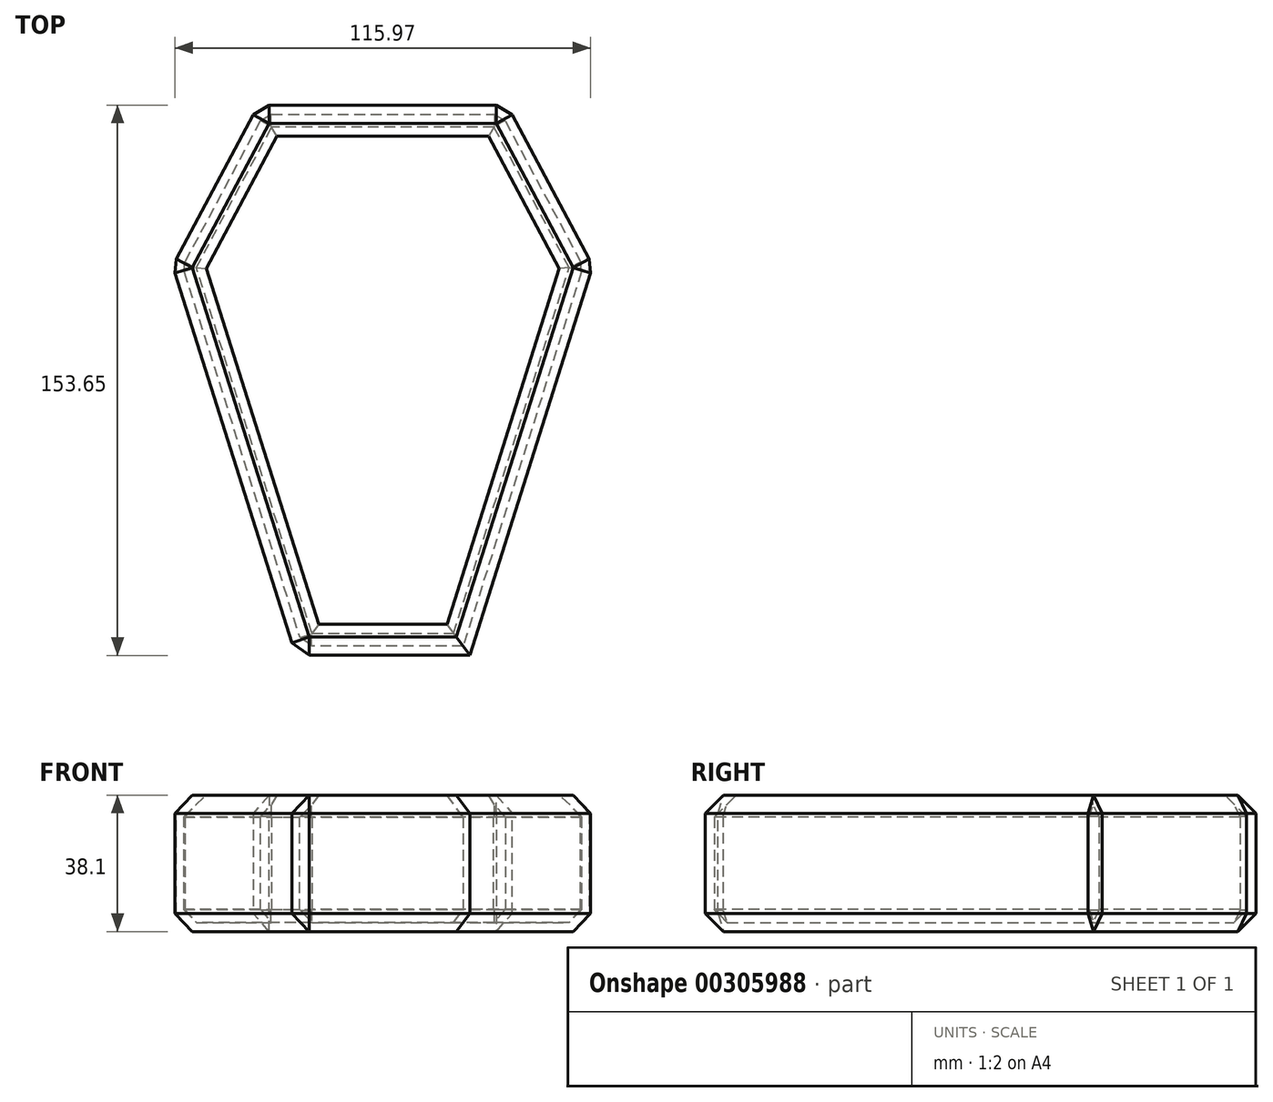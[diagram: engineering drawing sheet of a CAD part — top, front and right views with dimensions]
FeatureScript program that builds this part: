
annotation { "Feature Type Name" : "Feature", "Feature Type Description" : "" }
export const myFeature = defineFeature(function(context is Context, id is Id, definition is map)
    precondition{}
    {
        {
            var Q0;
            Q0=qCreatedBy(makeId("Top.planeOp"),FACE);
            var sketch = newSketch(context, id + "F0", { "sketchPlane" : qUnion([Q0])});
            skLineSegment(sketch, "E0", {"start": v(-34.33, -77.98) * mm, "end": v(-68.7, 30.86) * mm});
            skLineSegment(sketch, "E1", {"start": v(-68.7, 30.86) * mm, "end": v(-44.78, 75.67) * mm});
            skLineSegment(sketch, "E2", {"start": v(-34.33, -77.98) * mm, "end": v(-10.07, -77.98) * mm});
            skLineSegment(sketch, "E3", {"start": v(-44.78, 75.67) * mm, "end": v(-10.07, 75.67) * mm});
            skLineSegment(sketch, "E4.MirrorCS", {"start": v(24.63, 75.67) * mm, "end": v(-10.07, 75.67) * mm});
            skLineSegment(sketch, "E5.MirrorCS", {"start": v(48.56, 30.86) * mm, "end": v(24.63, 75.67) * mm});
            skLineSegment(sketch, "E6.MirrorCS", {"start": v(14.19, -77.98) * mm, "end": v(48.56, 30.86) * mm});
            skLineSegment(sketch, "E7.MirrorCS", {"start": v(14.19, -77.98) * mm, "end": v(-10.07, -77.98) * mm});
            skSolve(sketch);
        }
        {
            var Q0;
            Q0=makeQuery(id+"F0.imprint","IMPRINT",FACE,{"disambiguationData":[TD([[makeQuery(id+"F0.imprint","IMPRINT",EDGE,{"derivedFrom":sQuery(id+"F0.wireOp",EDGE,"E0")}),-1.0]])]});
            extrude(context, id + "F1", {"entities" : qUnion([Q0]), "depth" : 38.1 * mm});
        }
        {
            var Q0;
            Q0=makeQuery(id+"F1.opExtrude","CAP_EDGE",EDGE,{"disambiguationData":[OSD([sQuery(id+"F0.wireOp",EDGE,"E6.MirrorCS")])],"isStart":false});
            var Q1;
            Q1=makeQuery(id+"F1.opExtrude","CAP_EDGE",EDGE,{"disambiguationData":[OSD([sQuery(id+"F0.wireOp",EDGE,"E2"),sQuery(id+"F0.wireOp",EDGE,"E7.MirrorCS")])],"isStart":false});
            var Q2;
            Q2=makeQuery(id+"F1.opExtrude","CAP_EDGE",EDGE,{"disambiguationData":[OSD([sQuery(id+"F0.wireOp",EDGE,"E5.MirrorCS")])],"isStart":false});
            var Q3;
            Q3=makeQuery(id+"F1.opExtrude","CAP_EDGE",EDGE,{"disambiguationData":[OSD([sQuery(id+"F0.wireOp",EDGE,"E3"),sQuery(id+"F0.wireOp",EDGE,"E4.MirrorCS")])],"isStart":false});
            var Q4;
            Q4=makeQuery(id+"F1.opExtrude","CAP_EDGE",EDGE,{"disambiguationData":[OSD([sQuery(id+"F0.wireOp",EDGE,"E1")])],"isStart":false});
            var Q5;
            Q5=makeQuery(id+"F1.opExtrude","CAP_EDGE",EDGE,{"disambiguationData":[OSD([sQuery(id+"F0.wireOp",EDGE,"E0")])],"isStart":false});
            var Q6;
            Q6=makeQuery(id+"F1.opExtrude","CAP_EDGE",EDGE,{"disambiguationData":[OSD([sQuery(id+"F0.wireOp",EDGE,"E6.MirrorCS")])],"isStart":true});
            var Q7;
            Q7=makeQuery(id+"F1.opExtrude","CAP_EDGE",EDGE,{"disambiguationData":[OSD([sQuery(id+"F0.wireOp",EDGE,"E2"),sQuery(id+"F0.wireOp",EDGE,"E7.MirrorCS")])],"isStart":true});
            var Q8;
            Q8=makeQuery(id+"F1.opExtrude","SWEPT_FACE",FACE,{"disambiguationData":[OSD([sQuery(id+"F0.wireOp",EDGE,"E0")])]});
            var Q9;
            Q9=makeQuery(id+"F1.opExtrude","SWEPT_FACE",FACE,{"disambiguationData":[OSD([sQuery(id+"F0.wireOp",EDGE,"E1")])]});
            var Q10;
            Q10=makeQuery(id+"F1.opExtrude","SWEPT_FACE",FACE,{"disambiguationData":[OSD([sQuery(id+"F0.wireOp",EDGE,"E5.MirrorCS")])]});
            var Q11;
            Q11=makeQuery(id+"F1.opExtrude","SWEPT_FACE",FACE,{"disambiguationData":[OSD([sQuery(id+"F0.wireOp",EDGE,"E3"),sQuery(id+"F0.wireOp",EDGE,"E4.MirrorCS")])]});
            chamfer(context, id + "F2", {"entities" : qUnion([Q0, Q1, Q2, Q3, Q4, Q5, Q6, Q7, Q8, Q9, Q10, Q11]), "width" : 5.08 * mm, "tangentPropagation" : true});
        }
        {
            var Q0;
            Q0=makeQuery(id+"F1.opExtrude","CAP_FACE",FACE,{"disambiguationData":[OSD([sQuery(id+"F0.wireOp",EDGE,"E0"),sQuery(id+"F0.wireOp",EDGE,"E1"),sQuery(id+"F0.wireOp",EDGE,"E2"),sQuery(id+"F0.wireOp",EDGE,"E3"),sQuery(id+"F0.wireOp",EDGE,"E4.MirrorCS"),sQuery(id+"F0.wireOp",EDGE,"E5.MirrorCS"),sQuery(id+"F0.wireOp",EDGE,"E6.MirrorCS"),sQuery(id+"F0.wireOp",EDGE,"E7.MirrorCS")])],"isStart":false});
            shell(context, id + "F3", {"entities" : qUnion([Q0]), "thickness" : 2.54 * mm});
        }
    });
